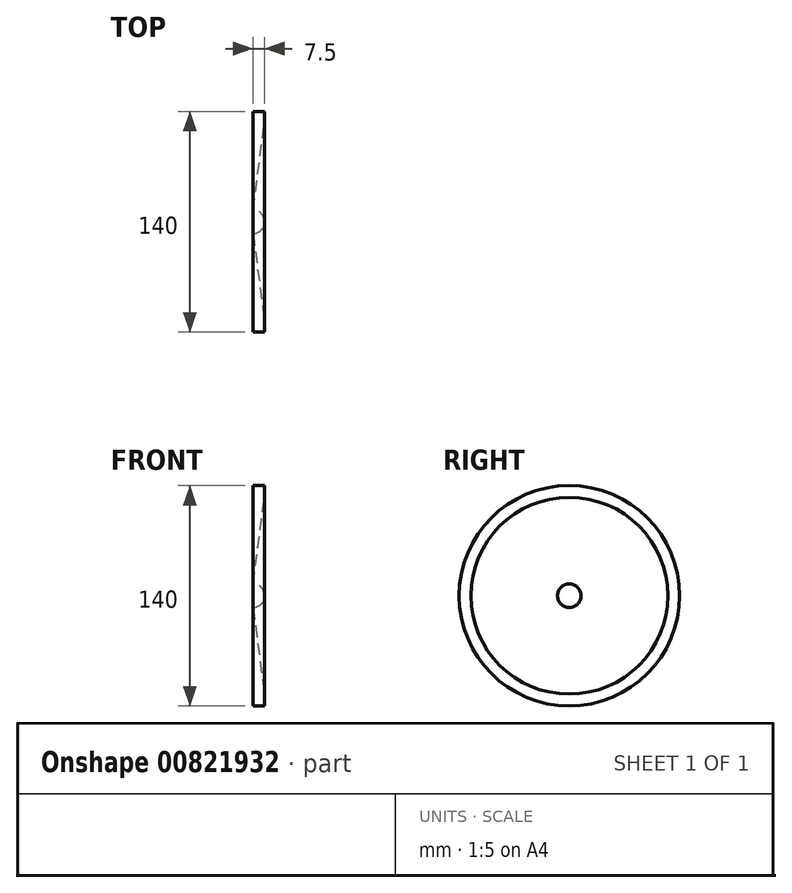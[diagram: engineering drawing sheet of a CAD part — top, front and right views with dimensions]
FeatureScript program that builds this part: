
annotation { "Feature Type Name" : "Feature", "Feature Type Description" : "" }
export const myFeature = defineFeature(function(context is Context, id is Id, definition is map)
    precondition{}
    {
        {
            var Q0;
            Q0=qCreatedBy(makeId("Front.planeOp"),FACE);
            var sketch = newSketch(context, id + "F0", { "sketchPlane" : qUnion([Q0])});
            skLineSegment(sketch, "E0", {"start": v(0, 0) * mm, "end": v(0, 70) * mm});
            skLineSegment(sketch, "E1", {"start": v(0, 70) * mm, "end": v(7.5, 70) * mm});
            skArc(sketch, "E2", {"start": v(0, 7.5) * mm, "mid": v(5.3, 5.3) * mm, "end": v(7.5, 0) * mm});
            skLineSegment(sketch, "E3", {"start": v(0, 0) * mm, "end": v(7.5, 0) * mm});
            skLineSegment(sketch, "E4", {"start": v(7.5, 70) * mm, "end": v(7.5, 62.5) * mm});
            skLineSegment(sketch, "E5", {"start": v(0, 7.5) * mm, "end": v(7.5, 62.5) * mm});
            skSolve(sketch);
        }
        {
            var Q0;
            Q0=qSketchRegion(id+"F0",true);
            var Q1;
            Q1=sQuery(id+"F0.wireOp",EDGE,"E3");
            revolve(context, id + "F1", {"surfaceOperationType" : NewSurfaceOperationType.NEW, "entities" : qUnion([Q0]), "axis" : qUnion([Q1]), "revolveType" : RevolveType.FULL});
        }
    });
